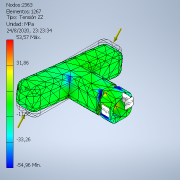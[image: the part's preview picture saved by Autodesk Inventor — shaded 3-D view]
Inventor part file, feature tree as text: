
AUTODESK INVENTOR PART (.ipt)
format: ipt  version: 2020.3 (Build 243373000, 373)  size: 270,848 bytes
history: native  units: in
note: dims shown in document units (in); Inventor stores cm internally (conversion verified against a paired STEP export)
features: extrude x4, sketch x4, fillet x3, plane x3, other x1
ambient origin geometry x8: Origin, YZ Plane, XZ Plane, XY Plane, X Axis, Y Axis, Z Axis, Center Point
bodies: Body1 (feature_tree)
feature tree (15):
  other  "Sólido1"
  extrude  "Extrusión1"  Depth=0.7874in
  fillet  "Empalme1"  Radius=3.5433in
  fillet  "Empalme2"  Radius=0.1969in
  plane  "Plano de trabajo1"
  extrude  "Extrusión2"  [1 undecoded]
  fillet  "Empalme3"  Radius=0.3937in
  plane  "Plano de trabajo2"
  extrude  "Extrusión3"  Depth=0.7874in
  extrude  "Extrusión4"  Depth=0.1969in
  plane  "Plano de trabajo3"
  sketch  "Boceto1"  dims[d0=0.7874in d1=0.7874in d2=3.5433in d3=0.0in d4=0.1969in]
  sketch  "Boceto2"  dims[d5=0.2756in d6=-0.3937in d7=0.3937in]
  sketch  "Boceto3"  dims[d8=0.7874in d9=0.7874in]
  sketch  "Boceto4"  dims[d10=1.9685in d11=0.0in d12=0.1969in d13=-0.3937in d14=0.3937in d15=0.5984in d16=1.1811in d17=0.0in d19=0.1496in d20=0.0in d21=-0.3937in d28=0.1969in d29=0.1969in d30=1.0907in]
note: 1 required parameter value undecoded (feature->parameter linkage not recoverable at this tier; creation-order binding heuristic only, values carry confidence <= 0.55)
